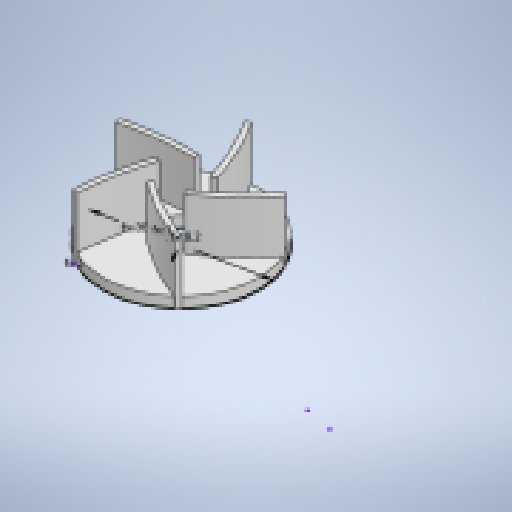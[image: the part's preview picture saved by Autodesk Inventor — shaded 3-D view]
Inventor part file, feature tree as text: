
AUTODESK INVENTOR PART (.ipt)
format: ipt  version: 2023.1 (Build 271208000, 208)  size: 290,816 bytes
history: native  units: in
note: dims shown in document units (in); Inventor stores cm internally (conversion verified against a paired STEP export)
features: extrude x2, other x1, sketch x1, pattern_circular x1
ambient origin geometry x8: Origin, YZ Plane, XZ Plane, XY Plane, X Axis, Y Axis, Z Axis, Center Point
bodies: Solid1 (feature_tree)
feature tree (5):
  other  "<userpath>\Documents\WaterPump\Parameters.xlsx"
  sketch  "Sketch1"  dims[d0=1.1811in d1=0.3228in d2=0.0787in d3=0.0in d10=0.0394in d11=0.0394in d12=0.4724in d13=0.0in d14=2.3622in d15=360.0deg]
  extrude  "Extrusion1"  Depth=0.4724in
  extrude  "Extrusion3"  Depth=0.0787in TaperAngle=0.0deg
  pattern_circular  "Circular Pattern2"  [2 undecoded]
note: 2 required parameter values undecoded (feature->parameter linkage not recoverable at this tier; creation-order binding heuristic only, values carry confidence <= 0.55)
